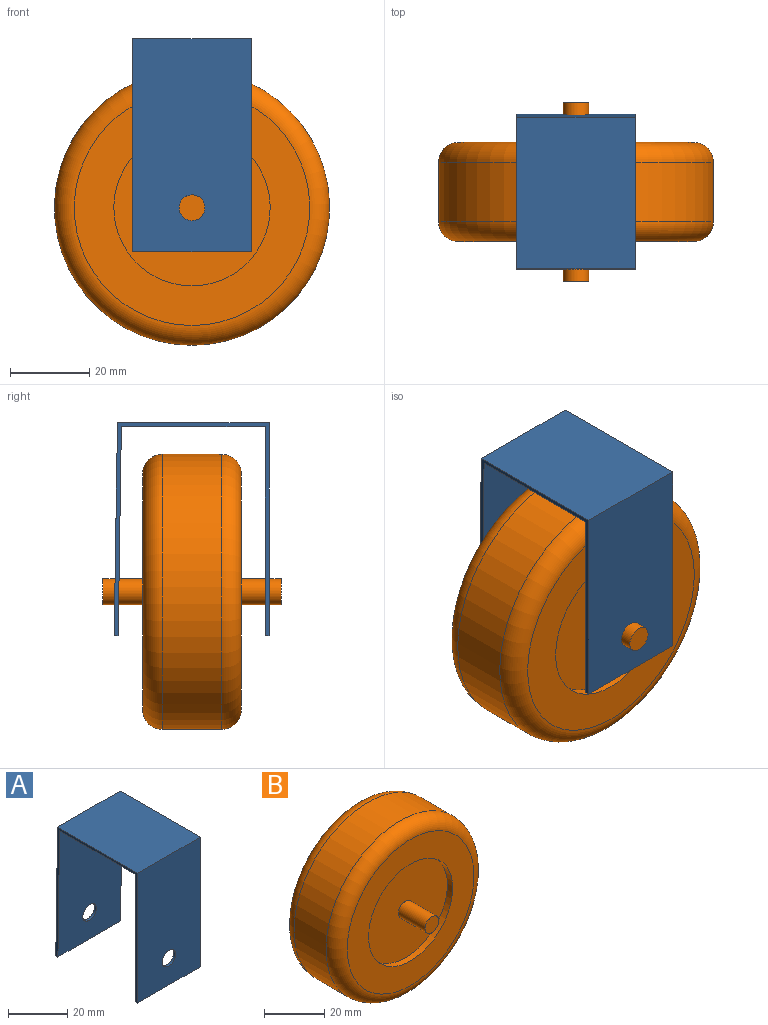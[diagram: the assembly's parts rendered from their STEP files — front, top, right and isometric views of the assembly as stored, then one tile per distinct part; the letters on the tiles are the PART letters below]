
ASSEMBLY  parts=2 mates=1
PART A: 12 faces, bbox 30x39.2x53.8 mm
  f0: plane 52.79x30mm, normal (0,1,0), area 1550.5mm2, adj f1,f7,f8,f9,f10
  f1: plane 36.34x30mm, normal (0,0,-1), area 1090.3mm2, adj f0,f2,f8,f9
  f2: plane 52.79x30mm, normal (0,-1,-0.02), area 1550.7mm2, adj f1,f3,f8,f9,f11
  f3: plane 30x1mm, normal (0,0,-1), area 30mm2, adj f2,f4,f8,f9
  f4: plane 53.79x30mm, normal (0,1,0.02), area 1580.7mm2, adj f3,f5,f8,f9,f11
  f5: plane 38.33x30mm, normal (0,0,1), area 1149.9mm2, adj f4,f6,f8,f9
  f6: plane 53.79x30mm, normal (0,-1,0), area 1580.5mm2, adj f5,f7,f8,f9,f10
  f7: plane 30x1mm, normal (0,0,-1), area 30mm2, adj f0,f6,f8,f9
  f8: plane 53.79x39.16mm, normal (1,0,0), area 143.9mm2, adj f0,f1,f2,f3,f4,f5,f6,f7
  f9: plane 53.79x39.16mm, normal (-1,0,0), area 143.9mm2, adj f0,f1,f2,f3,f4,f5,f6,f7
  f10: cylinder r=3.25mm len=6.5mm, axis (0,-1,0), area 20.4mm2, adj f0,f6
  f11: cylinder r=3.25mm len=6.5mm, axis (0,-1,0), area 20.4mm2, adj f2,f4
PART B: 13 faces, bbox 75.2x45x75.2 mm
  f0: plane 39.5x39.5mm, normal (0,-1,0), area 1192.2mm2, adj f3,f11
  f1: plane 39.5x39.5mm, normal (0,1,0), area 1192.2mm2, adj f2,f10
  f2: cylinder r=19.75mm len=39.5mm, axis (0,1,0), area 310.2mm2, adj f1,f6
  f3: cylinder r=19.75mm len=39.5mm, axis (0,1,0), area 310.2mm2, adj f0,f5
  f4: cylinder r=34.75mm len=69.5mm, axis (0,1,0), area 3275.1mm2, adj f7,f8
  f5: plane 59.5x59.5mm, normal (0,-1,0), area 1555.1mm2, adj f3,f8
  f6: plane 59.5x59.5mm, normal (0,1,0), area 1555.1mm2, adj f2,f7
  f7: torus R=29.75mm, axis (0,-1,0), area 1625.2mm2, adj f4,f6
  f8: torus R=29.75mm, axis (0,-1,0), area 1625.2mm2, adj f4,f5
  f9: plane 6.5x6.5mm, normal (0,1,0), area 33.2mm2, adj f10
  f10: cylinder r=3.25mm len=12.5mm, axis (0,1,0), area 255.3mm2, adj f1,f9
  f11: cylinder r=3.25mm len=12.5mm, axis (0,1,0), area 255.3mm2, adj f0,f12
  f12: plane 6.5x6.5mm, normal (0,-1,0), area 33.2mm2, adj f11
PLACE A t=(39.46,0,0)mm
PLACE B t=(39.46,0.13,0)mm
MATE revolute B.f10 <-> A.f10  axis (0,-1,0) through (39.46,-22.37,0)mm
